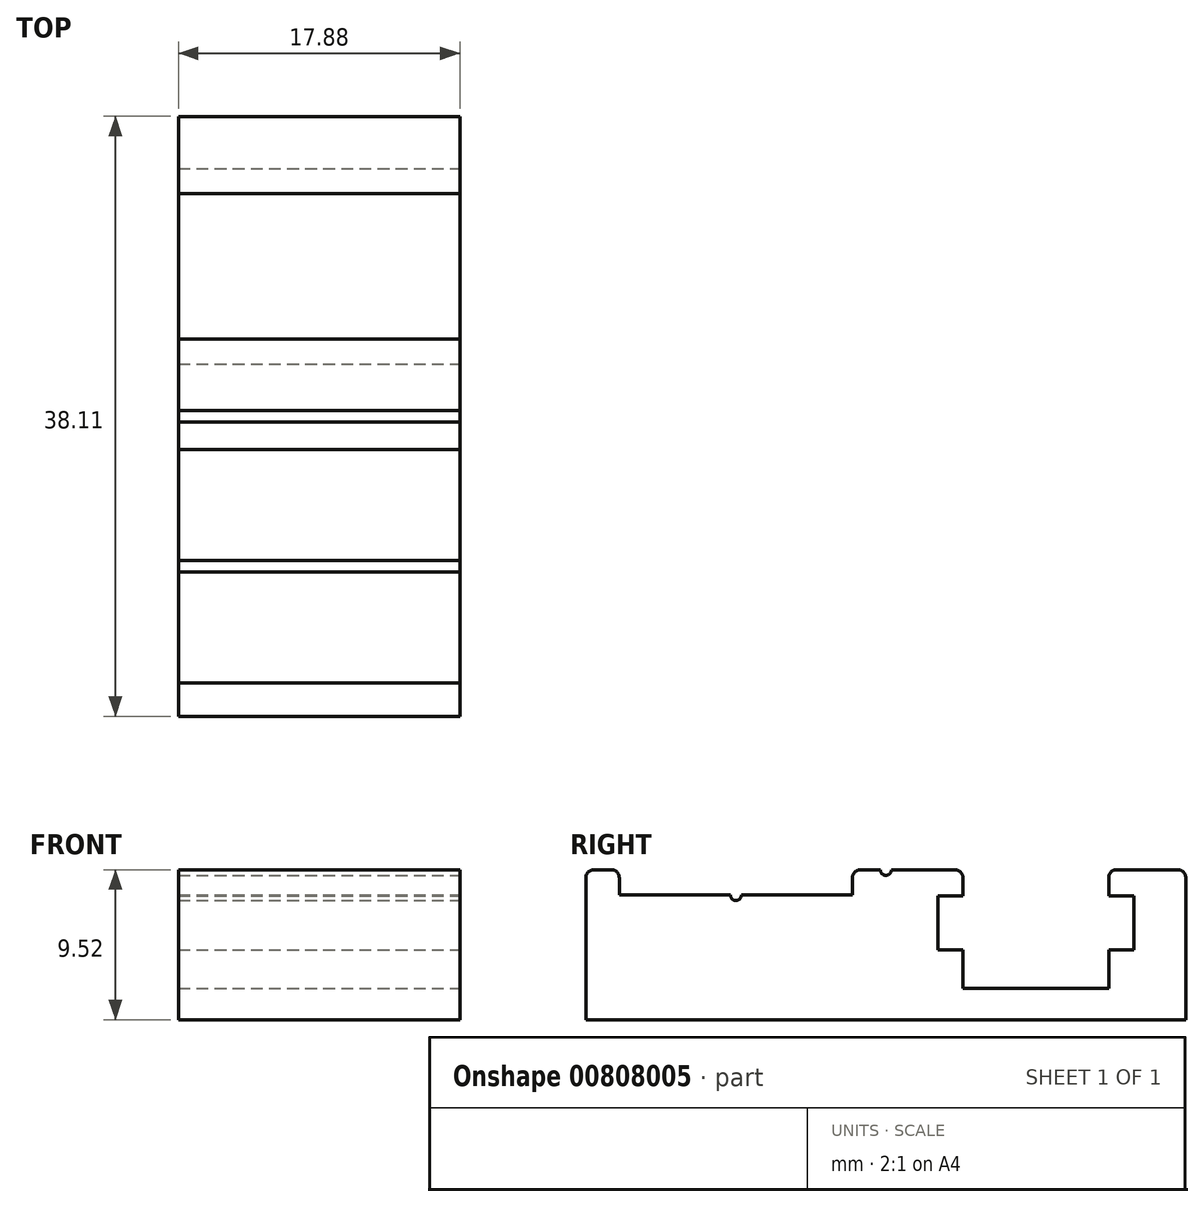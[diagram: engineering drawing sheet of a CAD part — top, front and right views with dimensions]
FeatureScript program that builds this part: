
annotation { "Feature Type Name" : "Feature", "Feature Type Description" : "" }
export const myFeature = defineFeature(function(context is Context, id is Id, definition is map)
    precondition{}
    {
        {
            var Q0;
            Q0=qCreatedBy(makeId("Right.planeOp"),FACE);
            var sketch = newSketch(context, id + "F0", { "sketchPlane" : qUnion([Q0])});
            skLineSegment(sketch, "E0.0.0", {"start": v(-9.52, -7.25) * mm, "end": v(9.53, -7.25) * mm});
            skLineSegment(sketch, "E0.0.1", {"start": v(9.53, -7.25) * mm, "end": v(9.53, 1.76) * mm});
            skLineSegment(sketch, "E0.0.2", {"start": v(9.02, 2.27) * mm, "end": v(5.14, 2.27) * mm});
            skLineSegment(sketch, "E0.0.3", {"start": v(4.63, 1.76) * mm, "end": v(4.63, 0.62) * mm});
            skLineSegment(sketch, "E0.0.4", {"start": v(4.63, 0.62) * mm, "end": v(6.22, 0.62) * mm});
            skLineSegment(sketch, "E0.0.5", {"start": v(6.22, 0.62) * mm, "end": v(6.22, -2.82) * mm});
            skLineSegment(sketch, "E0.0.6", {"start": v(6.22, -2.82) * mm, "end": v(4.63, -2.82) * mm});
            skLineSegment(sketch, "E0.0.7", {"start": v(4.63, -2.82) * mm, "end": v(4.63, -5.27) * mm});
            skLineSegment(sketch, "E0.0.8", {"start": v(4.63, -5.27) * mm, "end": v(-4.63, -5.27) * mm});
            skLineSegment(sketch, "E0.0.9", {"start": v(-4.63, -5.27) * mm, "end": v(-4.63, -2.82) * mm});
            skLineSegment(sketch, "E0.0.10", {"start": v(-4.63, -2.82) * mm, "end": v(-6.22, -2.82) * mm});
            skLineSegment(sketch, "E0.0.11", {"start": v(-6.22, -2.82) * mm, "end": v(-6.22, 0.62) * mm});
            skLineSegment(sketch, "E0.0.12", {"start": v(-6.22, 0.62) * mm, "end": v(-4.63, 0.62) * mm});
            skLineSegment(sketch, "E0.0.13", {"start": v(-4.63, 0.62) * mm, "end": v(-4.63, 1.76) * mm});
            skLineSegment(sketch, "E0.0.14", {"start": v(-5.14, 2.27) * mm, "end": v(-9.17, 2.27) * mm});
            skLineSegment(sketch, "E0.0.15", {"start": v(-9.52, 1.92) * mm, "end": v(-9.52, -7.25) * mm});
            skLineSegment(sketch, "E1", {"start": v(-9.52, -7.25) * mm, "end": v(-28.57, -7.25) * mm});
            skLineSegment(sketch, "E2", {"start": v(-28.57, -7.25) * mm, "end": v(-28.57, 1.76) * mm});
            skLineSegment(sketch, "E3", {"start": v(-28.07, 2.27) * mm, "end": v(-26.96, 2.27) * mm});
            skLineSegment(sketch, "E4", {"start": v(-26.46, 1.76) * mm, "end": v(-26.46, 0.67) * mm});
            skLineSegment(sketch, "E5", {"start": v(-26.46, 0.67) * mm, "end": v(-19.4, 0.67) * mm});
            skLineSegment(sketch, "E6", {"start": v(-11.64, 0.67) * mm, "end": v(-11.64, 1.76) * mm});
            skLineSegment(sketch, "E7", {"start": v(-11.14, 2.27) * mm, "end": v(-9.88, 2.27) * mm});
            skArc(sketch, "E8", {"start": v(-19.4, 0.67) * mm, "mid": v(-19.05, 0.32) * mm, "end": v(-18.7, 0.67) * mm});
            skLineSegment(sketch, "E9.trimOffspring", {"start": v(-18.7, 0.67) * mm, "end": v(-11.64, 0.67) * mm});
            skArc(sketch, "E10", {"start": v(-9.88, 2.27) * mm, "mid": v(-9.52, 1.92) * mm, "end": v(-9.17, 2.27) * mm});
            skPoint(sketch, "E11.visualSharp", {"position": v(9.53, 2.27) * mm});
            skArc(sketch, "E11.filletArc", {"start": v(9.53, 1.76) * mm, "mid": v(9.38, 2.12) * mm, "end": v(9.02, 2.27) * mm});
            skPoint(sketch, "E12.visualSharp", {"position": v(-28.57, 2.27) * mm});
            skArc(sketch, "E12.filletArc", {"start": v(-28.07, 2.27) * mm, "mid": v(-28.43, 2.12) * mm, "end": v(-28.57, 1.76) * mm});
            skPoint(sketch, "E13.visualSharp", {"position": v(-11.64, 2.27) * mm});
            skArc(sketch, "E13.filletArc", {"start": v(-11.14, 2.27) * mm, "mid": v(-11.5, 2.12) * mm, "end": v(-11.64, 1.76) * mm});
            skPoint(sketch, "E14.visualSharp", {"position": v(-4.63, 2.27) * mm});
            skArc(sketch, "E14.filletArc", {"start": v(-4.63, 1.76) * mm, "mid": v(-4.78, 2.12) * mm, "end": v(-5.14, 2.27) * mm});
            skPoint(sketch, "E15.visualSharp", {"position": v(-26.46, 2.27) * mm});
            skArc(sketch, "E15.filletArc", {"start": v(-26.46, 1.76) * mm, "mid": v(-26.6, 2.12) * mm, "end": v(-26.96, 2.27) * mm});
            skPoint(sketch, "E16.visualSharp", {"position": v(4.63, 2.27) * mm});
            skArc(sketch, "E16.filletArc", {"start": v(5.14, 2.27) * mm, "mid": v(4.78, 2.12) * mm, "end": v(4.63, 1.76) * mm});
            skSolve(sketch);
        }
        {
            var Q0;
            Q0 = qSketchRegion(id + "F0", true);
            extrude(context, id + "F1", {"entities" : qUnion([Q0]), "oppositeDirection" : true, "depth" : (17 + (7 / 8)) * mm, "offsetDistance" : 25.4 * mm});
        }
    });
